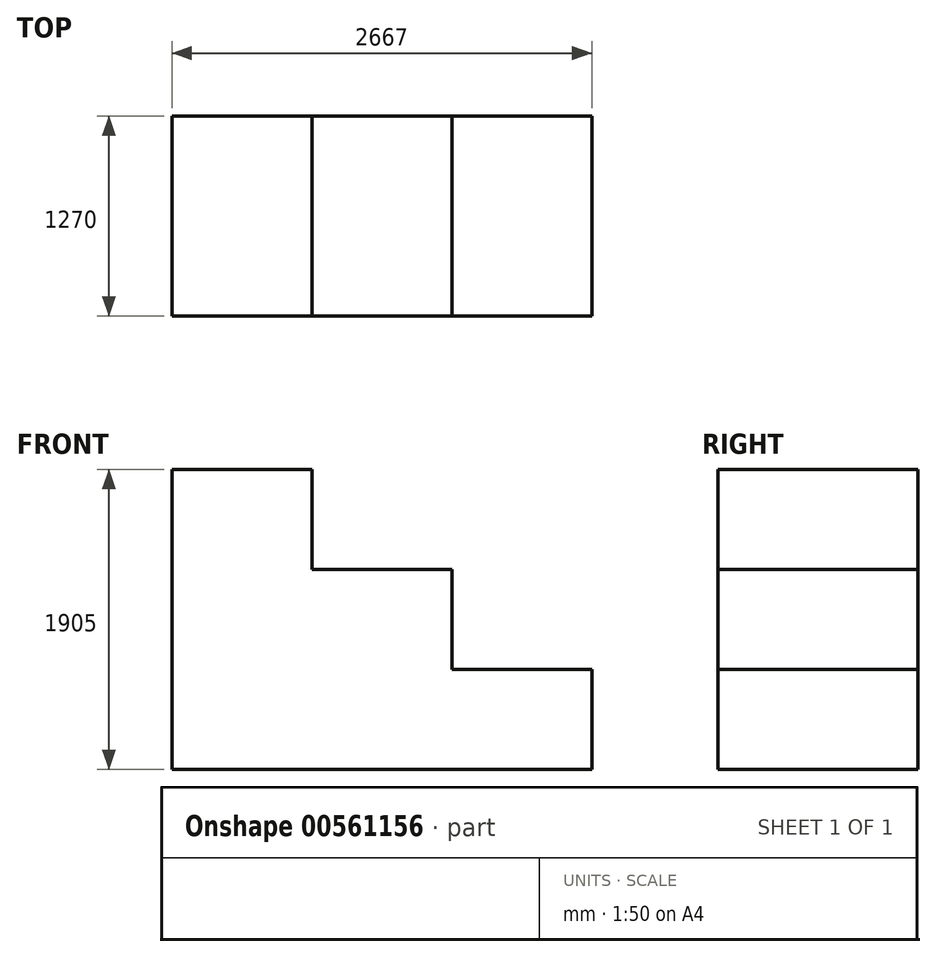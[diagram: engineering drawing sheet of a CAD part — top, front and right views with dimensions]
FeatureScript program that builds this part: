
annotation { "Feature Type Name" : "Feature", "Feature Type Description" : "" }
export const myFeature = defineFeature(function(context is Context, id is Id, definition is map)
    precondition{}
    {
        {
            var Q0;
            Q0=qCreatedBy(makeId("Top.planeOp"),FACE);
            var sketch = newSketch(context, id + "F0", { "sketchPlane" : qUnion([Q0])});
            skLineSegment(sketch, "E0.bottom", {"start": v(-1333.5, 635) * mm, "end": v(1333.5, 635) * mm});
            skLineSegment(sketch, "E0.top", {"start": v(-1333.5, -635) * mm, "end": v(1333.5, -635) * mm});
            skLineSegment(sketch, "E0.left", {"start": v(-1333.5, 635) * mm, "end": v(-1333.5, -635) * mm});
            skLineSegment(sketch, "E0.right", {"start": v(1333.5, 635) * mm, "end": v(1333.5, -635) * mm});
            skPoint(sketch, "E0.middle", {"position": v(0, 0) * mm});
            skSolve(sketch);
        }
        {
            var Q0;
            Q0 = qSketchRegion(id + "F0", true);
            extrude(context, id + "F1", {"entities" : qUnion([Q0]), "depth" : 1905 * mm, "offsetDistance" : 25.4 * mm});
        }
        {
            var Q0;
            Q0=makeQuery(id+"F1.opExtrude","SWEPT_FACE",FACE,{"disambiguationData":[OSD([sQuery(id+"F0.wireOp",EDGE,"E0.bottom")])]});
            var sketch = newSketch(context, id + "F2", { "sketchPlane" : qUnion([Q0])});
            skLineSegment(sketch, "E1", {"start": v(-1333.5, 0) * mm, "end": v(-1333.5, 635) * mm});
            skLineSegment(sketch, "E2", {"start": v(-1333.5, 635) * mm, "end": v(-444.5, 635) * mm});
            skLineSegment(sketch, "E3", {"start": v(-444.5, 635) * mm, "end": v(-444.5, 1270) * mm});
            skLineSegment(sketch, "E4", {"start": v(-444.5, 1270) * mm, "end": v(444.5, 1270) * mm});
            skLineSegment(sketch, "E5", {"start": v(444.5, 1270) * mm, "end": v(444.5, 1905) * mm});
            skLineSegment(sketch, "E6", {"start": v(444.5, 1905) * mm, "end": v(1333.5, 1905) * mm});
            skSolve(sketch);
        }
        {
            var Q0;
            Q0 = qSketchRegion(id + "F2", true);
            var Q1;
            {var subQ1=sQuery(id+"F2.wireOp",EDGE,"E2");Q1=makeQuery(id+"F2.imprint","IMPRINT",FACE,{"disambiguationData":[TD([[makeQuery(id+"F2.imprint","IMPRINT",EDGE,{"derivedFrom":subQ1}),1.0]])]});}
            extrude(context, id + "F3", {"entities" : qUnion([Q0, Q1]), "operationType" : NewBodyOperationType.REMOVE, "endBound" : BoundingType.THROUGH_ALL, "oppositeDirection" : true, "depth" : 1270 * mm, "offsetDistance" : 25.4 * mm});
        }
    });
